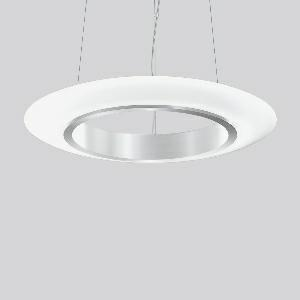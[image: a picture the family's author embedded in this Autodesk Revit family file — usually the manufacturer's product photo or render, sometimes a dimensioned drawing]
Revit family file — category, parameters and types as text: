
# Revit family: ring_of_fire_p_311570_004_1_730_ccd8
name_source: partatom
category: Lighting Fixtures
units: mm (PartAtom-declared; Revit-internal decimal feet)

## family parameters
Cut with Voids When Loaded = No
Host = Face
Light Source = No
Part Type = Normal
Room Calculation Point = No
Round Connector Dimension = Use Diameter
Shared = No

## types (1)
- RING OF FIRE P (1 x LED Modul 840, 4150 lm, 4000)
    Apparent Load = 37 VA
    CIE Flux Codes = 43 73 90 55 100
    Color Rendering = 80
    Color Temperature = 4000
    Default Elevation = 1800 mm
    Description = Series: RING OF FIRE
A uniquely shaped pendant luminaire with elliptical glass. Supporting ring made of anodised aluminium. Canopy aluminium anodised. Opal glass: mouth-blown, satin finish. Suitable for pendant. 3-point steel cable suspension, steplessly adjustable. Special lengths available on request. For pendant lengths of up to 2 m, power is supplied through a suspension cable. For pendant lengths of 2 m and more, power must be supplied through a separate cable. Converter integrated in the canopy. With Casambi smart+free Bluetooth control for wireless network and operation using Android / iOS devices, free app available for download. 
Colour: anodised aluminium
Diameter: 690 mm
Height: 81 mm
Suspension length: 500-1200 mm
Lamp: LED
Socket: without socket
Colour temperature: 4000K
Colour rendering index (CRI): 80
System power: 37 W
Rated luminous flux: 4150 lm
Luminous efficiency: 112 lm/W
Control gear: Dimmable Bluetooth converter
Protection class: I
Type of protection: IP 20
    Height = 81 mm
    Lamp = 1 x LED Modul 840
    Lamp Light Flux = 4150 lm
    Lamp count = 1
    Length = 690 mm
    Lifetime = 50000 h
    Luminous efficacy = 112 lm/W
    Manufacturer = RZB
    ModVariant = No
    Model = 311570.004.1.730
    Mounting Place = Ceiling
    Mounting Type = Pendant
    Number of Poles = 1
    OnlyDefault = Yes
    Power Factor = 1
    Product Name = RING OF FIRE P
    Product group = Pendant luminaires
    ProductGroupID = 902
    Protection Class = Protection class I
    Protection Degree = IP 20
    RLX_Detail_Level = 1
    RLX_Emergency_Light_Flux = 0 lm
    RLX_Emergency_Type = 0
    RLX_Emergency_Type_DB = No
    RlxData = <blob elided: 30485 chars, md5=e9e4504b>
    Socket = socket
    Standby Power = 0 W
    System Light Flux = 4150 lm
    System Power = 37 W
    Type Comments = Product without accessories
    Type Image = 311570.004.jpg
    URL = http://relux.com
    VarID = ---
    Voltage = 230 V
    Voltage Range = 220-240 V
    Weight = 0.00 kg
    Width = 0 mm  [stored 0 ft]

note: [stored X ft] marks values corroborated as IEEE doubles in the binary element streams (Revit-internal decimal feet)

## geometry (parser evidence)
native form markers: Blend x4, Sweep x14
no freeform markers — native parametric forms only
